# Revit family: 2014-ES_Puerta-Seccional_AEPA
name_source: partatom
category: Puertas
revit_build: Autodesk Revit 2014 (Build: 20130308_1515(x64)
units: mm (PartAtom-declared; Revit-internal decimal feet)

## types (1)
- Puerta Seccional 4000x4000mm
    Alt. Real Lama = 243 mm
    Altura = 4000 mm  [stored 13.1234 ft]
    Altura Cuelgues Carril = 244 mm
    Altura Def Lama = 243 mm
    Altura Fijaciones Techo = 409 mm
    Altura Hueco = 4390 mm
    Altura Nivel Techo Maquinaria = 300 mm
    Altura Perfil Vertical sobre dintel = 390 mm
    Anchura = 4000 mm  [stored 13.1234 ft]
    Anchura Hueco = 4140 mm  [stored 13.5827 ft]
    Anchura de marco = 75 mm  [stored 0.246063 ft]
    Asociación- AEPA = http://www.aepa.ws
    Bimetica = www.bimetica.com
    Cantidad Piezas Fijacion = 4
    Cierre de muro = Por anfitrión
    Colección = Biblioteca BIM AEPA
    Creado por = Bimetica Parametric Design Services S.L.
    Descripción = Puerta Seccional Genérica AEPA
    Desfase exterior = 0 mm  [stored 0 ft]
    Desfase interior = 0 mm  [stored 0 ft]
    Estructura = Aluminio- Puerta Generica- AEPA
    Fabricante - CONTROLSA = http://www.controlsa.com
    Fabricante - ROLLTORE PORTIS = http://www.portis.es
    Fecha Revisión de Contenido = 15/12/2014
    Fecha de Caducidad de Información = 01/01/2016
    Función = Interior
    Gomas = Gomas- Puerta Generica- AEPA
    Información Técnica = http://bimetica.com
    Lama = Panel Sandwich- Puerta Generica- AEPA
    Largo Carril Maquinaria = 5022 mm
    Longitud Horizontal Guia Inferior = 4000 mm  [stored 13.1234 ft]
    Longitud Horizontal Guia Superior = 4022 mm
    Masterformat Código = 08 36 13
    Masterformat Descripción = Sectional Doors
    Mitad Longitud Puerta = 2000 mm  [stored 6.56168 ft]
    Mitad Longitud Real Lama = 2020 mm
    Modelo = Genérico AEPA
    N Piezas = 16 mm
    Numero lamas = 16
    Omniclass Código = 23-17 11 13 25 13
    Omniclass Título = Sectional Overhead Metal Doors
    Piezas - Redondeo = 16
    Proyección marco ext. = 25 mm  [stored 0.082021 ft]
    Proyección marco int. = 25 mm  [stored 0.082021 ft]
    Redondeo Lamas = 16
    Representación Horizontal L. H. Guia Inferior = 4300 mm
    UNSPSC Categoría = Rolling garage door
    UNSPSC Código = 30172108
    URL = http://www.aepa.ws
    Uniclass 2.0 Código = 25-30-20-76
    Uniclass 2.0 Descripción = Sectional overhead doorset systems

note: [stored X ft] marks values corroborated as IEEE doubles in the binary element streams (Revit-internal decimal feet)

## geometry (parser evidence)
native form markers: Blend x2, Sweep x2
no freeform markers — native parametric forms only
